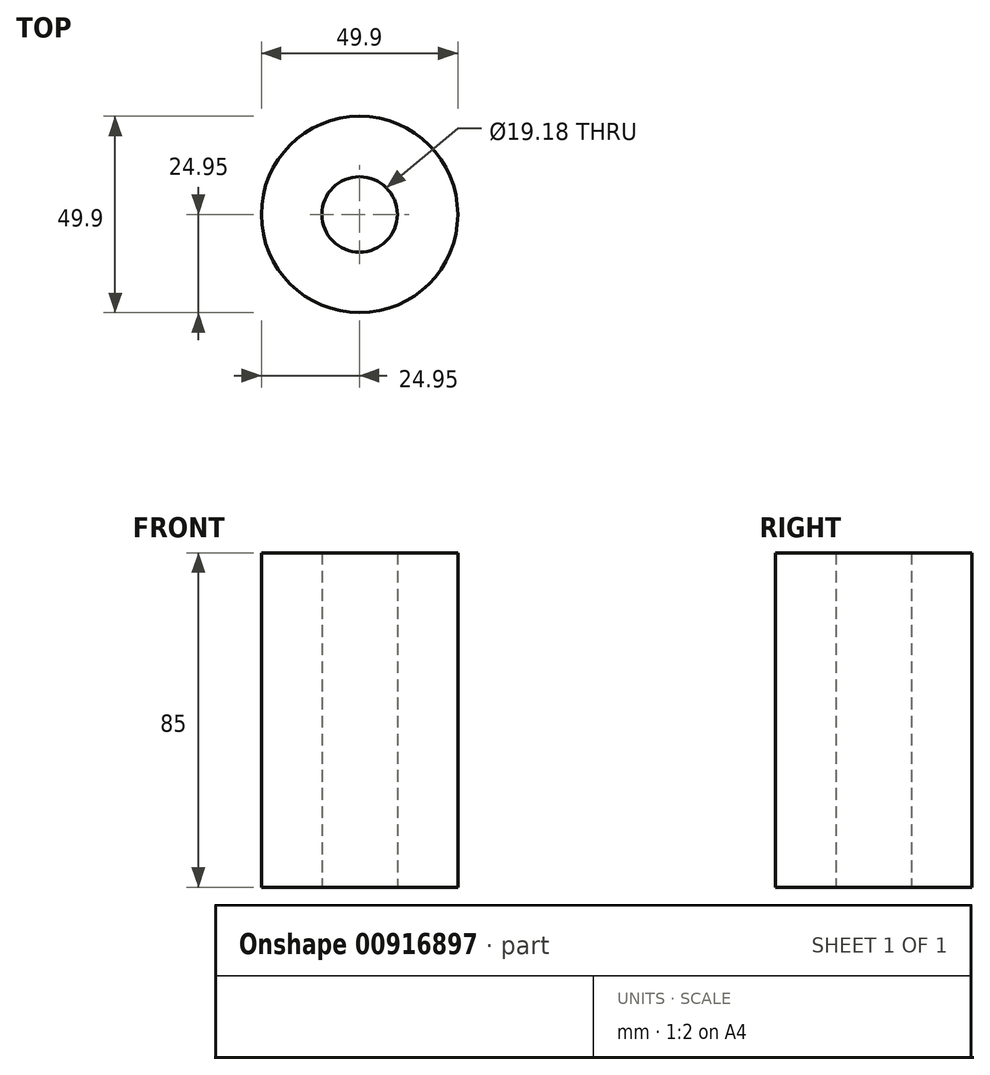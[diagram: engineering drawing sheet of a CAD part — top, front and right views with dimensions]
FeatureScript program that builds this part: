
annotation { "Feature Type Name" : "Feature", "Feature Type Description" : "" }
export const myFeature = defineFeature(function(context is Context, id is Id, definition is map)
    precondition{}
    {
        {
            var Q0;
            Q0=qCreatedBy(makeId("Top.planeOp"),FACE);
            var sketch = newSketch(context, id + "F0", { "sketchPlane" : qUnion([Q0])});
            skCircle(sketch, "E0", {"center": v(0, 0) * mm, "radius": 24.95 * mm});
            skSolve(sketch);
        }
        {
            var Q0;
            Q0=makeQuery(id+"F0.imprint","IMPRINT",FACE,{"disambiguationData":[TD([[makeQuery(id+"F0.imprint","IMPRINT",EDGE,{"derivedFrom":sQuery(id+"F0.wireOp",EDGE,"E0")}),1.0]])]});
            extrude(context, id + "F1", {"entities" : qUnion([Q0]), "depth" : 75.1 * mm, "offsetDistance" : 25 * mm});
        }
        {
            var Q0;
            Q0=makeQuery(id+"F1.opExtrude","CAP_FACE",FACE,{"disambiguationData":[OSD([sQuery(id+"F0.wireOp",EDGE,"E0")])],"isStart":true});
            var sketch = newSketch(context, id + "F2", { "sketchPlane" : qUnion([Q0])});
            skCircle(sketch, "E1", {"center": v(0, 0) * mm, "radius": 9.57 * mm});
            skSolve(sketch);
        }
        {
            var Q0;
            Q0=makeQuery(id+"F2.imprint","IMPRINT",FACE,{"disambiguationData":[TD([[makeQuery(id+"F2.imprint","IMPRINT",EDGE,{"derivedFrom":sQuery(id+"F2.wireOp",EDGE,"E1")}),1.0]])]});
            var Q1;
            Q1=makeQuery(id+"F1.opExtrude","CAP_FACE",FACE,{"disambiguationData":[OSD([sQuery(id+"F0.wireOp",EDGE,"E0")])],"isStart":true});
            var Q2;
            Q2=makeQuery(id+"F2.imprint","IMPRINT",FACE,{"disambiguationData":[TD([[makeQuery(id+"F2.imprint","IMPRINT",EDGE,{"derivedFrom":sQuery(id+"F2.wireOp",EDGE,"E1")}),-1.0]])]});
            extrude(context, id + "F3", {"entities" : qUnion([Q0, Q1, Q2]), "operationType" : NewBodyOperationType.ADD, "oppositeDirection" : true, "depth" : 85 * mm, "offsetDistance" : 25 * mm});
        }
        {
            var Q0;
            {var subQ0=sQuery(id+"F0.wireOp",EDGE,"E0");Q0=makeQuery(id+"F3.opExtrude","CAP_FACE",FACE,{"disambiguationData":[OSD([subQ0]),TDD([makeQuery(id+"F1.opExtrude","CAP_FACE",FACE,{"disambiguationData":[OSD([subQ0])],"isStart":true})])],"isStart":false});}
            var sketch = newSketch(context, id + "F4", { "sketchPlane" : qUnion([Q0])});
            skCircle(sketch, "E2", {"center": v(0, 0) * mm, "radius": 9.5 * mm});
            skSolve(sketch);
        }
        {
            var Q0;
            Q0=makeQuery(id+"F4.imprint","IMPRINT",FACE,{"disambiguationData":[TD([[makeQuery(id+"F4.imprint","IMPRINT",EDGE,{"derivedFrom":sQuery(id+"F4.wireOp",EDGE,"E2")}),1.0]])]});
            extrude(context, id + "F5", {"entities" : qUnion([Q0]), "operationType" : NewBodyOperationType.ADD, "oppositeDirection" : true, "depth" : 84.9 * mm, "offsetDistance" : 25 * mm});
        }
        {
            var Q0;
            Q0=makeQuery(id+"F1.opExtrude","CAP_FACE",FACE,{"disambiguationData":[OSD([sQuery(id+"F0.wireOp",EDGE,"E0")])],"isStart":true});
            var sketch = newSketch(context, id + "F6", { "sketchPlane" : qUnion([Q0])});
            skCircle(sketch, "E3", {"center": v(0, 0) * mm, "radius": 9.52 * mm});
            skSolve(sketch);
        }
        {
            var Q0;
            Q0=makeQuery(id+"F6.imprint","IMPRINT",FACE,{"disambiguationData":[TD([[makeQuery(id+"F6.imprint","IMPRINT",EDGE,{"derivedFrom":sQuery(id+"F6.wireOp",EDGE,"E3")}),1.0]])]});
            extrude(context, id + "F7", {"entities" : qUnion([Q0]), "operationType" : NewBodyOperationType.ADD, "oppositeDirection" : true, "depth" : 84.7 * mm, "offsetDistance" : 25 * mm});
        }
        {
            var Q0;
            Q0=qCreatedBy(makeId("Top.planeOp"),FACE);
            var sketch = newSketch(context, id + "F8", { "sketchPlane" : qUnion([Q0])});
            skCircle(sketch, "E4", {"center": v(0, 0) * mm, "radius": 9.59 * mm});
            skSolve(sketch);
        }
        {
            var Q0;
            Q0=makeQuery(id+"F8.imprint","IMPRINT",FACE,{"disambiguationData":[TD([[makeQuery(id+"F8.imprint","IMPRINT",EDGE,{"derivedFrom":sQuery(id+"F8.wireOp",EDGE,"E4")}),1.0]])]});
            extrude(context, id + "F9", {"entities" : qUnion([Q0]), "operationType" : NewBodyOperationType.REMOVE, "depth" : 94.3 * mm, "offsetDistance" : 25 * mm});
        }
    });
